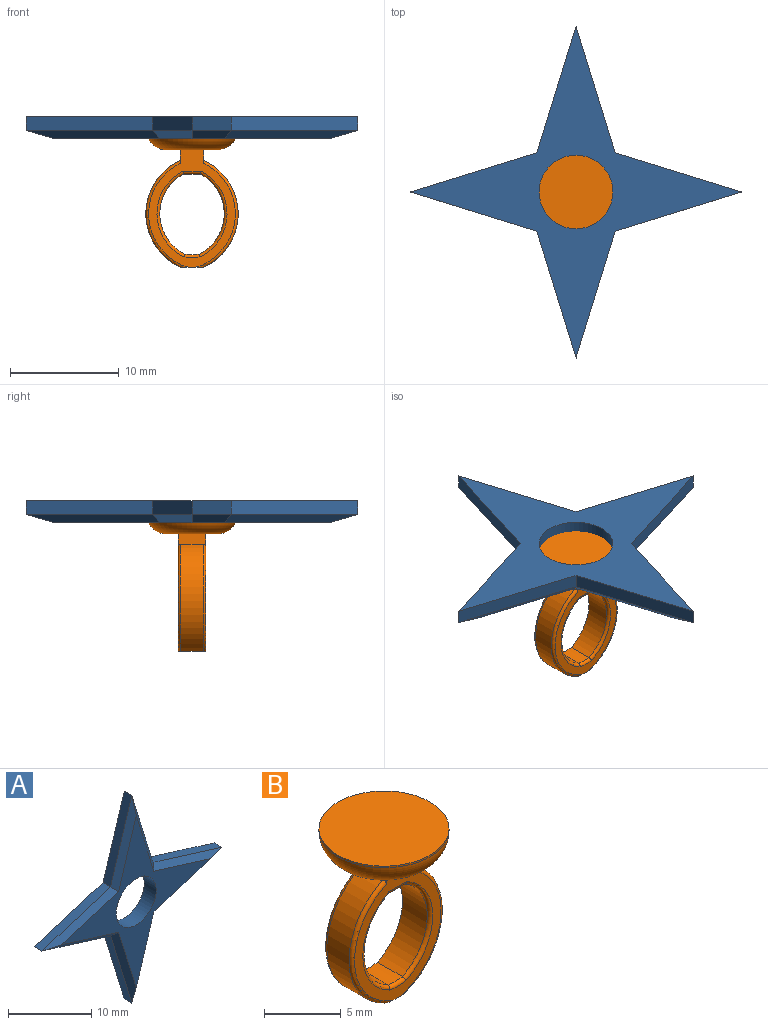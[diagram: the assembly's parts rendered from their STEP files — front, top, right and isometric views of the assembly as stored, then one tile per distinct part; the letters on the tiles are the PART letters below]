
ASSEMBLY  parts=2 mates=1
PART A: 19 faces, bbox 30.5x2x30.5 mm
  f0: plane 11.65x3.59mm, normal (0.96,0,-0.29), area 15.5mm2, adj f1,f7,f10,f18
  f1: plane 11.65x3.59mm, normal (0.29,0,-0.96), area 15.5mm2, adj f0,f2,f10,f16
  f2: plane 11.65x3.59mm, normal (0.29,0,0.96), area 15.5mm2, adj f1,f3,f10,f14
  f3: plane 11.65x3.59mm, normal (0.96,0,0.29), area 15.5mm2, adj f2,f4,f10,f12
  f4: plane 11.65x3.59mm, normal (-0.96,0,0.29), area 15.5mm2, adj f3,f5,f10,f11
  f5: plane 11.65x3.59mm, normal (-0.29,0,0.96), area 15.5mm2, adj f4,f6,f10,f13
  f6: plane 11.65x3.59mm, normal (-0.29,0,-0.96), area 15.5mm2, adj f5,f7,f10,f15
  f7: plane 11.65x3.59mm, normal (-0.96,0,-0.29), area 15.5mm2, adj f0,f6,f10,f17
  f8: cylinder r=3.39mm len=6.77mm, axis (0,1,0), area 43.2mm2, adj f9,f10
  f9: plane 25.31x25.31mm, normal (0,-1,0), area 114.9mm2, adj f8,f11,f12,f13,f14,f15,f16,f17
  f10: plane 30.48x30.48mm, normal (0,1,0), area 182.9mm2, adj f0,f1,f2,f3,f4,f5,f6,f7
  f11: plane 12.26x3.59mm, normal (-0.68,-0.71,0.21), area 12mm2, adj f4,f9,f12,f13
  f12: plane 12.26x3.59mm, normal (0.68,-0.71,0.21), area 12mm2, adj f3,f9,f11,f14
  f13: plane 12.26x3.59mm, normal (-0.21,-0.71,0.68), area 12mm2, adj f5,f9,f11,f15
  f14: plane 12.26x3.59mm, normal (0.21,-0.71,0.68), area 12mm2, adj f2,f9,f12,f16
  f15: plane 12.26x3.59mm, normal (-0.21,-0.71,-0.68), area 12mm2, adj f6,f9,f13,f17
  f16: plane 12.26x3.59mm, normal (0.21,-0.71,-0.68), area 12mm2, adj f1,f9,f14,f18
  f17: plane 12.26x3.59mm, normal (-0.68,-0.71,-0.21), area 12mm2, adj f7,f9,f15,f18
  f18: plane 12.26x3.59mm, normal (0.68,-0.71,-0.21), area 12mm2, adj f0,f9,f16,f17
PART B: 24 faces, bbox 9.4x9.2x13.5 mm
  f0: cylinder r=4.23mm len=8.47mm, axis (0,0,1), area 3.4mm2, adj f2,f3
  f1: plane 4.66x4.66mm, normal (0,0,-1), area 11.6mm2, adj f3,f8,f9,f13,f14
  f2: plane 8.47x8.47mm, normal (0,0,1), area 56.3mm2, adj f0
  f3: torus R=2.33mm, axis (0,0,-1), area 66.6mm2, adj f0,f1
  f4: plane 2.03x1.54mm, normal (0,0,-1), area 3.1mm2, adj f5,f12,f15,f22
  f5: cylinder r=4.14mm len=7.61mm, axis (0,1,0), area 20.8mm2, adj f4,f6,f14,f15,f21
  f6: cylinder r=3.76mm len=2.29mm, axis (0,1,0), area 3mm2, adj f5,f12,f14,f19
  f7: cylinder r=5.41mm len=9.84mm, axis (0,1,0), area 25.1mm2, adj f8,f11,f16,f18
  f8: plane 2.59x1.28mm, normal (1,0,0), area 2.4mm2, adj f1,f7,f13,f14,f16,f18
  f9: plane 2.59x1.28mm, normal (-1,0,0), area 2.4mm2, adj f1,f10,f13,f14,f17,f23
  f10: cylinder r=5.41mm len=9.84mm, axis (0,1,0), area 25.1mm2, adj f9,f11,f17,f23
  f11: plane 2.54x2.13mm, normal (0,0,-1), area 5.3mm2, adj f7,f10,f13,f14,f16,f17,f18,f23
  f12: cylinder r=4.14mm len=7.61mm, axis (0,1,0), area 20.8mm2, adj f4,f6,f14,f15,f20
  f13: plane 10.8x7.96mm, normal (0,-1,0), area 21.8mm2, adj f1,f8,f9,f11,f18,f19,f20,f21
  f14: plane 10.8x7.96mm, normal (0,1,0), area 27.1mm2, adj f1,f5,f6,f8,f9,f11,f12,f15
  f15: cylinder r=0.25mm len=1.54mm, axis (1,0,0), area 0.5mm2, adj f4,f5,f12,f14
  f16: torus R=5.15mm, axis (0,-1,0), area 4.9mm2, adj f7,f8,f11,f14
  f17: torus R=5.15mm, axis (0,-1,0), area 4.9mm2, adj f9,f10,f11,f14
  f18: torus R=5.15mm, axis (0,-1,0), area 4.9mm2, adj f7,f8,f11,f13
  f19: torus R=4.02mm, axis (0,-1,0), area 0.6mm2, adj f6,f13,f20,f21
  f20: torus R=4.39mm, axis (0,-1,0), area 3.7mm2, adj f12,f13,f19,f22
  f21: torus R=4.39mm, axis (0,-1,0), area 3.7mm2, adj f5,f13,f19,f22
  f22: cylinder r=0.25mm len=1.66mm, axis (-1,0,0), area 0.6mm2, adj f4,f13,f20,f21
  f23: torus R=5.15mm, axis (0,-1,0), area 4.9mm2, adj f9,f10,f11,f13
PLACE A rot(axis=(1,0,0),90deg) t=(6.89,6.53,16.89)mm
PLACE B t=(6.89,6.53,46.1)mm
MATE fastened A.f8 <-> B.f0  axis (0,0,1) through (6.89,6.53,16.89)mm
